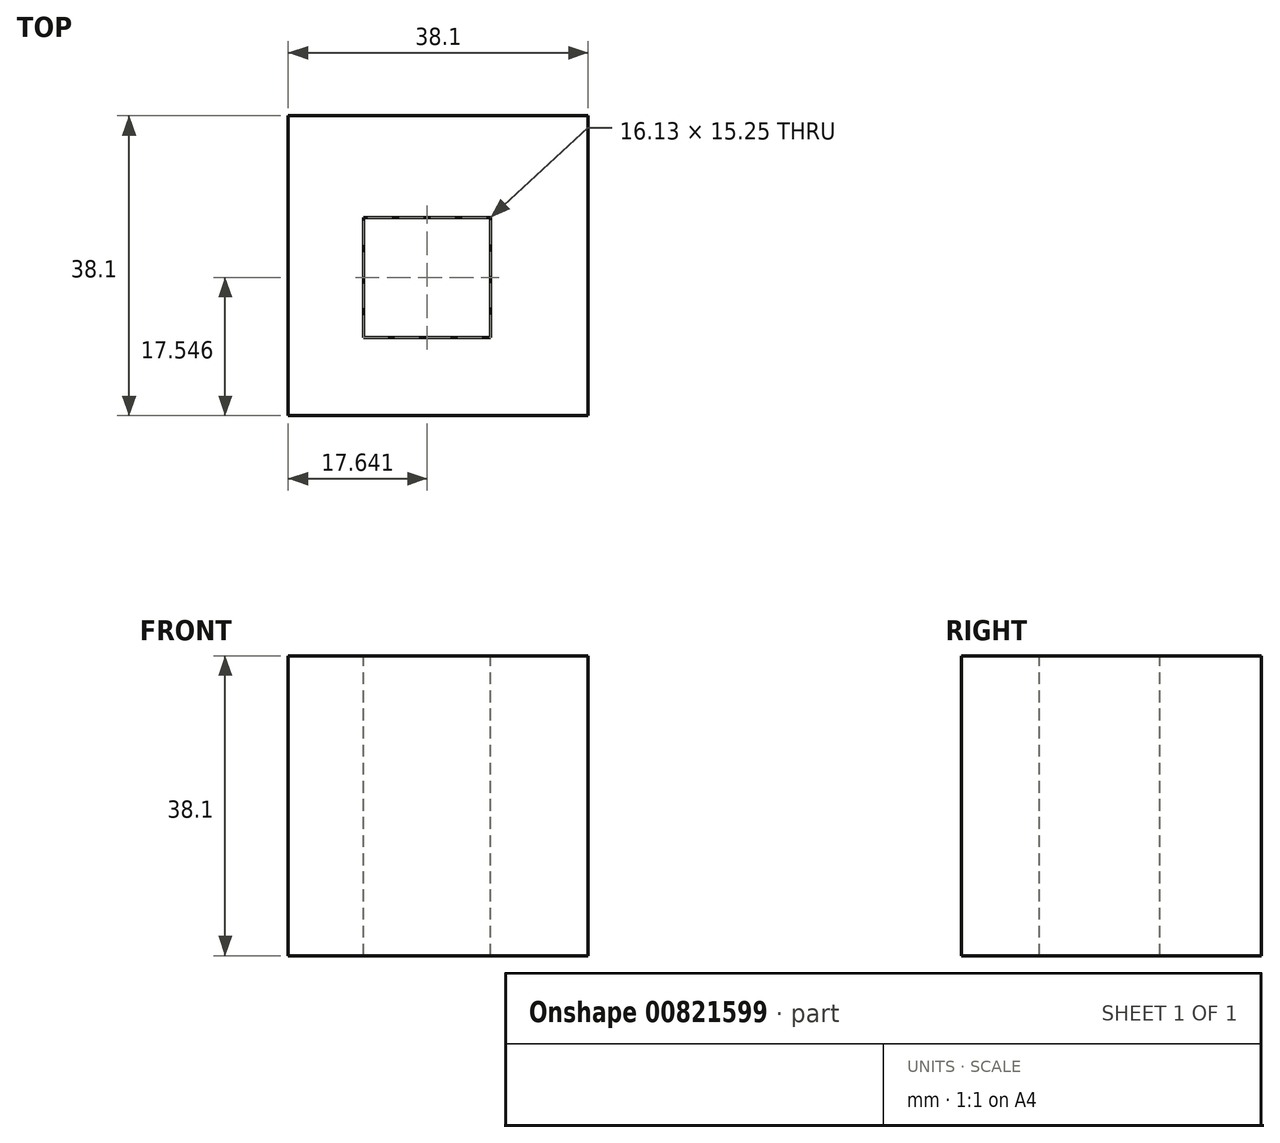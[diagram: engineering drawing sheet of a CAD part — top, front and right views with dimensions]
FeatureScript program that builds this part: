
annotation { "Feature Type Name" : "Feature", "Feature Type Description" : "" }
export const myFeature = defineFeature(function(context is Context, id is Id, definition is map)
    precondition{}
    {
        {
            var Q0;
            Q0=qCreatedBy(makeId("Front.planeOp"),FACE);
            var sketch = newSketch(context, id + "F0", { "sketchPlane" : qUnion([Q0])});
            skLineSegment(sketch, "E0.bottom", {"start": v(-24, 38.84) * mm, "end": v(14.1, 38.84) * mm});
            skLineSegment(sketch, "E0.top", {"start": v(-24, 0.74) * mm, "end": v(14.1, 0.74) * mm});
            skLineSegment(sketch, "E0.left", {"start": v(-24, 38.84) * mm, "end": v(-24, 0.74) * mm});
            skLineSegment(sketch, "E0.right", {"start": v(14.1, 38.84) * mm, "end": v(14.1, 0.74) * mm});
            skSolve(sketch);
        }
        {
            var Q0;
            Q0=makeQuery(id+"F0.imprint","IMPRINT",FACE,{"disambiguationData":[TD([[makeQuery(id+"F0.imprint","IMPRINT",EDGE,{"derivedFrom":sQuery(id+"F0.wireOp",EDGE,"E0.bottom")}),-1.0]])]});
            extrude(context, id + "F1", {"entities" : qUnion([Q0]), "depth" : 38.1 * mm, "offsetDistance" : 25.4 * mm});
        }
        {
            var Q0;
            Q0=makeQuery(id+"F1.opExtrude","SWEPT_FACE",FACE,{"disambiguationData":[OSD([sQuery(id+"F0.wireOp",EDGE,"E0.bottom")])]});
            var sketch = newSketch(context, id + "F2", { "sketchPlane" : qUnion([Q0])});
            skLineSegment(sketch, "E1.bottom", {"start": v(1.7, -28.18) * mm, "end": v(-14.42, -28.18) * mm});
            skLineSegment(sketch, "E1.top", {"start": v(1.7, -12.93) * mm, "end": v(-14.42, -12.93) * mm});
            skLineSegment(sketch, "E1.left", {"start": v(1.7, -28.18) * mm, "end": v(1.7, -12.93) * mm});
            skLineSegment(sketch, "E1.right", {"start": v(-14.42, -28.18) * mm, "end": v(-14.42, -12.93) * mm});
            skPoint(sketch, "E1.middle", {"position": v(-6.36, -20.55) * mm});
            skSolve(sketch);
        }
        {
            var Q0;
            Q0=makeQuery(id+"F2.imprint","IMPRINT",FACE,{"disambiguationData":[TD([[makeQuery(id+"F2.imprint","IMPRINT",EDGE,{"derivedFrom":sQuery(id+"F2.wireOp",EDGE,"E1.bottom")}),-1.0]])]});
            extrude(context, id + "F3", {"entities" : qUnion([Q0]), "operationType" : NewBodyOperationType.REMOVE, "oppositeDirection" : true, "depth" : 50.8 * mm, "offsetDistance" : 25.4 * mm});
        }
    });
